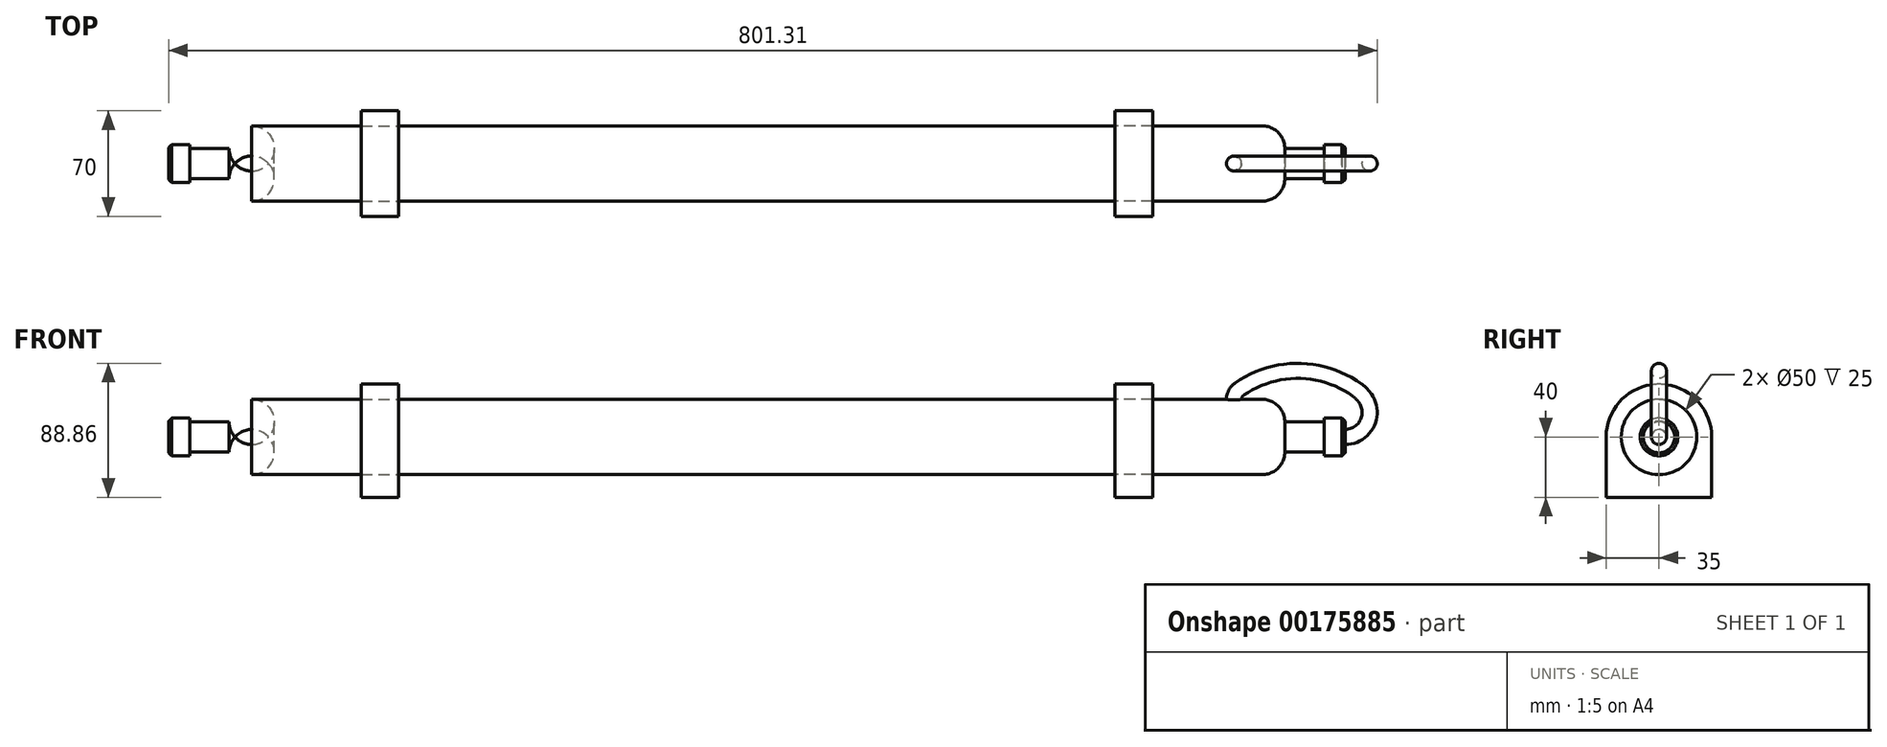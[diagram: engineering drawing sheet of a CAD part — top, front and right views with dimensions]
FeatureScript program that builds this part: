
annotation { "Feature Type Name" : "Feature", "Feature Type Description" : "" }
export const myFeature = defineFeature(function(context is Context, id is Id, definition is map)
    precondition{}
    {
        {
            var Q0;
            Q0=qCreatedBy(makeId("Right.planeOp"),FACE);
            var sketch = newSketch(context, id + "F0", { "sketchPlane" : qUnion([Q0])});
            skCircle(sketch, "E0", {"center": v(0, 0) * mm, "radius": 25 * mm});
            skSolve(sketch);
        }
        {
            var Q0;
            Q0 = qSketchRegion(id + "F0", true);
            extrude(context, id + "F1", {"entities" : qUnion([Q0]), "endBound" : BoundingType.SYMMETRIC, "depth" : 700 * mm});
        }
        {
            var Q0;
            Q0=makeQuery(id+"F1.opExtrude","CAP_EDGE",EDGE,{"disambiguationData":[OSD([sQuery(id+"F0.wireOp",EDGE,"E0")])],"isStart":true});
            var Q1;
            Q1=makeQuery(id+"F1.opExtrude","CAP_EDGE",EDGE,{"disambiguationData":[OSD([sQuery(id+"F0.wireOp",EDGE,"E0")])],"isStart":false});
            fillet(context, id + "F2", {"entities" : qUnion([Q0, Q1]), "radius" : 15 * mm, "tangentPropagation" : true, "allowEdgeOverflow" : false});
        }
        {
            var Q0;
            Q0=makeQuery(id+"F1.opExtrude","CAP_FACE",FACE,{"disambiguationData":[OSD([sQuery(id+"F0.wireOp",EDGE,"E0")])],"isStart":true});
            extrude(context, id + "F3", {"entities" : qUnion([Q0]), "depth" : 26 * mm});
        }
        {
            var Q0;
            Q0=makeQuery(id+"F3.opExtrude","CAP_FACE",FACE,{"disambiguationData":[OSD([sQuery(id+"F0.wireOp",EDGE,"E0")])],"isStart":false});
            var sketch = newSketch(context, id + "F4", { "sketchPlane" : qUnion([Q0])});
            skCircle(sketch, "E1", {"center": v(0, 0) * mm, "radius": 12.5 * mm});
            skSolve(sketch);
        }
        {
            var Q0;
            Q0 = qSketchRegion(id + "F4", true);
            extrude(context, id + "F5", {"entities" : qUnion([Q0]), "operationType" : NewBodyOperationType.ADD, "depth" : 14 * mm});
        }
        {
            var Q0;
            Q0=makeQuery(id+"F3.opExtrude","SWEPT_BODY",BODY,{"disambiguationData":[OSD([sQuery(id+"F0.wireOp",EDGE,"E0")])]});
            var Q1;
            Q1=qCreatedBy(makeId("Right.planeOp"),FACE);
            mirror(context, id + "F6", {"operationType" : NewBodyOperationType.ADD, "entities" : qUnion([Q0]), "mirrorPlane" : qUnion([Q1])});
        }
        {
            var Q0;
            Q0=qCreatedBy(makeId("Front.planeOp"),FACE);
            var sketch = newSketch(context, id + "F7", { "sketchPlane" : qUnion([Q0])});
            skLineSegment(sketch, "E2.0", {"start": v(390, -12.5) * mm, "end": v(390, 12.5) * mm, "construction": true});
            skArc(sketch, "E3", {"start": v(390, 0) * mm, "mid": v(404.46, 8.77) * mm, "end": v(403.37, 25.64) * mm});
            skLineSegment(sketch, "E4", {"start": v(390, 0) * mm, "end": v(335, 0) * mm, "construction": true});
            skArc(sketch, "E5", {"start": v(403.37, 25.64) * mm, "mid": v(400.86, 28.66) * mm, "end": v(397.87, 31.2) * mm});
            skArc(sketch, "E6", {"start": v(397.87, 31.2) * mm, "mid": v(358.98, 43.86) * mm, "end": v(319.9, 31.8) * mm});
            skArc(sketch, "E7", {"start": v(319.9, 31.8) * mm, "mid": v(317.28, 28.84) * mm, "end": v(316.34, 25) * mm});
            skLineSegment(sketch, "E8.0", {"start": v(335, -25) * mm, "end": v(335, 25) * mm, "construction": true});
            skLineSegment(sketch, "E9", {"start": v(316.34, 25) * mm, "end": v(316.34, -25) * mm, "construction": true});
            skLineSegment(sketch, "E10", {"start": v(316.34, 25) * mm, "end": v(316.34, 15.2) * mm});
            skSolve(sketch);
        }
        {
            var Q0;
            Q0=makeQuery(id+"F6.opPattern","COPY",FACE,{"derivedFrom":makeQuery(id+"F5.opExtrude","CAP_FACE",FACE,{"disambiguationData":[OSD([sQuery(id+"F4.wireOp",EDGE,"E1")])],"isStart":false}),"instanceName":"1"});
            var sketch = newSketch(context, id + "F8", { "sketchPlane" : qUnion([Q0])});
            skCircle(sketch, "E11", {"center": v(0, 0) * mm, "radius": 5 * mm});
            skSolve(sketch);
        }
        {
            var Q0;
            Q0 = qSketchRegion(id + "F8", true);
            var Q1;
            Q1 = qConstructionFilter(qBodyType(qCreatedBy(id + "F7" ,EDGE), BodyType.WIRE), ConstructionObject.NO);
            sweep(context, id + "F9", {"operationType" : NewBodyOperationType.ADD, "profiles" : qUnion([Q0]), "path" : qUnion([Q1])});
        }
        {
            var Q0;
            Q0=makeQuery(id+"F5.opExtrude","CAP_EDGE",EDGE,{"disambiguationData":[OSD([sQuery(id+"F4.wireOp",EDGE,"E1")])],"isStart":false});
            var Q1;
            Q1=makeQuery(id+"F6.opPattern","COPY",EDGE,{"derivedFrom":makeQuery(id+"F5.opExtrude","CAP_EDGE",EDGE,{"disambiguationData":[OSD([sQuery(id+"F4.wireOp",EDGE,"E1")])],"isStart":false}),"instanceName":"1"});
            chamfer(context, id + "F10", {"entities" : qUnion([Q0, Q1]), "width" : 2 * mm, "tangentPropagation" : true});
        }
        {
            var Q0;
            Q0=qCreatedBy(makeId("Right.planeOp"),FACE);
            cPlane(context, id + "F11", {"entities" : qUnion([Q0]), "cplaneType" : CPlaneType.OFFSET, "offset" : 250 * mm, "width" : 150 * mm, "height" : 150 * mm});
        }
        {
            var Q0;
            Q0=qCreatedBy(id+"F11.planeOp",FACE);
            var sketch = newSketch(context, id + "F12", { "sketchPlane" : qUnion([Q0])});
            skCircle(sketch, "E12.0", {"center": v(0, 0) * mm, "radius": 25 * mm});
            skLineSegment(sketch, "E13.bottom", {"start": v(-35, 0) * mm, "end": v(35, 0) * mm, "construction": true});
            skLineSegment(sketch, "E13.top", {"start": v(-35, -40) * mm, "end": v(35, -40) * mm});
            skLineSegment(sketch, "E13.left", {"start": v(-35, 0) * mm, "end": v(-35, -40) * mm});
            skLineSegment(sketch, "E13.right", {"start": v(35, 0) * mm, "end": v(35, -40) * mm});
            skPoint(sketch, "E13.middle", {"position": v(0, -20) * mm});
            skArc(sketch, "E14", {"start": v(35, 0) * mm, "mid": v(0, 35) * mm, "end": v(-35, 0) * mm});
            skSolve(sketch);
        }
        {
            var Q0;
            Q0 = qSketchRegion(id + "F12", true);
            extrude(context, id + "F13", {"entities" : qUnion([Q0]), "endBound" : BoundingType.SYMMETRIC, "depth" : 25 * mm});
        }
        {
            var Q0;
            Q0=makeQuery(id+"F13.opExtrude","SWEPT_BODY",BODY,{"disambiguationData":[OSD([sQuery(id+"F12.wireOp",EDGE,"E12.0"),sQuery(id+"F12.wireOp",EDGE,"E13.top"),sQuery(id+"F12.wireOp",EDGE,"E13.left"),sQuery(id+"F12.wireOp",EDGE,"E13.right"),sQuery(id+"F12.wireOp",EDGE,"E14")])]});
            var Q1;
            Q1=qCreatedBy(makeId("Right.planeOp"),FACE);
            mirror(context, id + "F14", {"entities" : qUnion([Q0]), "mirrorPlane" : qUnion([Q1])});
        }
    });
